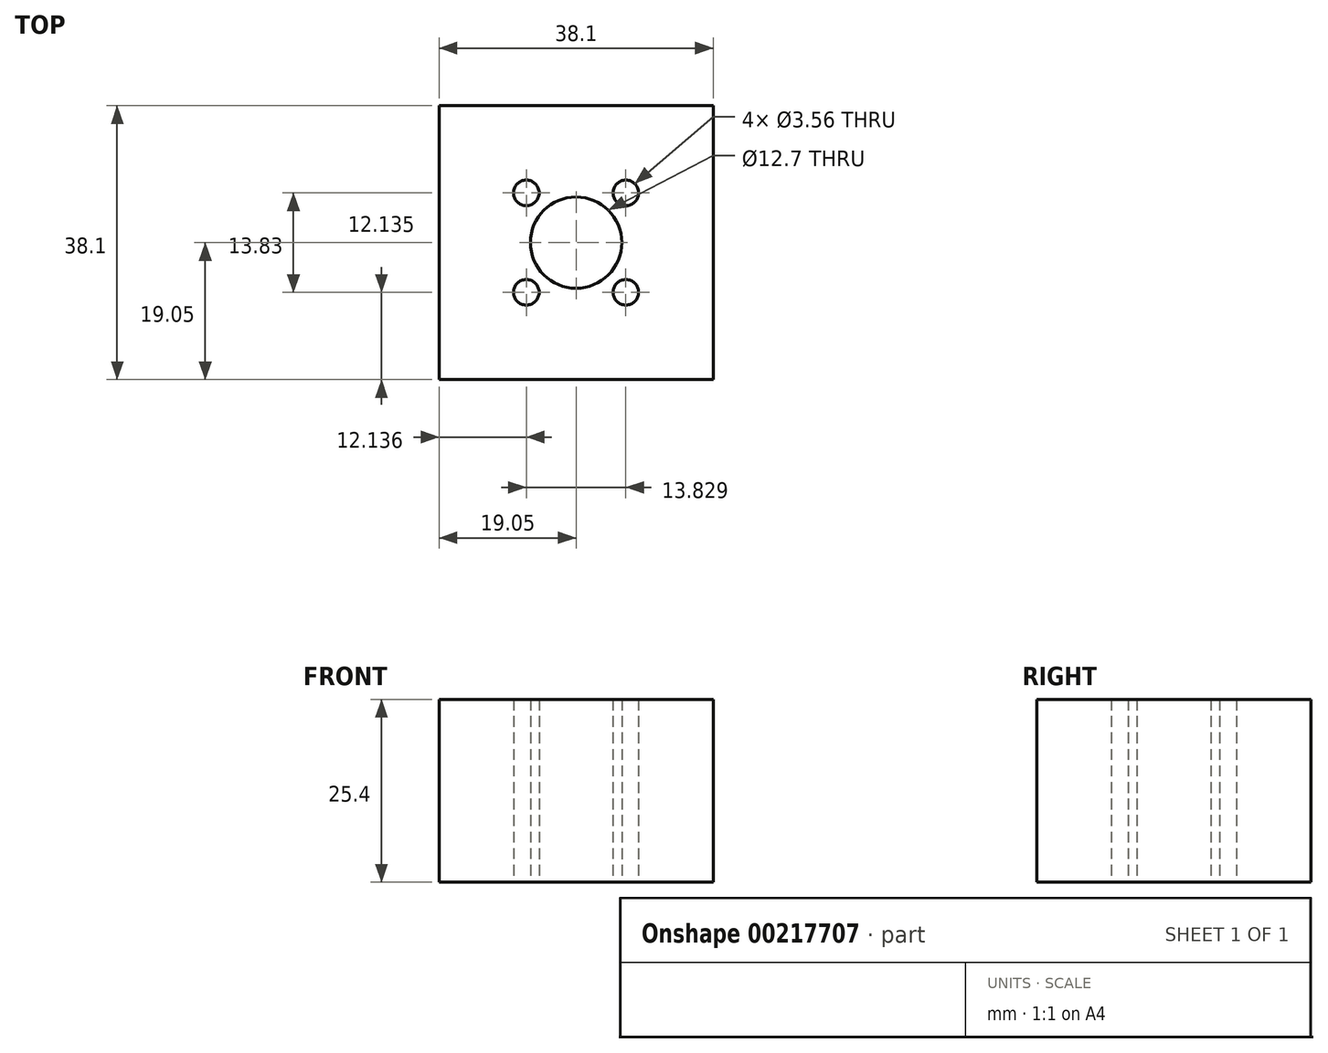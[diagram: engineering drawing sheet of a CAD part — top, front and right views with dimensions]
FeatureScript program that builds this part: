
annotation { "Feature Type Name" : "Feature", "Feature Type Description" : "" }
export const myFeature = defineFeature(function(context is Context, id is Id, definition is map)
    precondition{}
    {
        {
            var Q0;
            Q0=qCreatedBy(makeId("Top.planeOp"),FACE);
            var sketch = newSketch(context, id + "F0", { "sketchPlane" : qUnion([Q0])});
            skLineSegment(sketch, "E0.bottom", {"start": v(-19.05, 19.05) * mm, "end": v(19.05, 19.05) * mm});
            skLineSegment(sketch, "E0.top", {"start": v(-19.05, -19.05) * mm, "end": v(19.05, -19.05) * mm});
            skLineSegment(sketch, "E0.left", {"start": v(-19.05, 19.05) * mm, "end": v(-19.05, -19.05) * mm});
            skLineSegment(sketch, "E0.right", {"start": v(19.05, 19.05) * mm, "end": v(19.05, -19.05) * mm});
            skPoint(sketch, "E0.middle", {"position": v(0, 0) * mm});
            skCircle(sketch, "E1", {"center": v(0, 0) * mm, "radius": 6.35 * mm});
            skCircle(sketch, "E2", {"center": v(-6.91, 6.92) * mm, "radius": 1.78 * mm});
            skCircle(sketch, "E3", {"center": v(6.91, 6.92) * mm, "radius": 1.78 * mm});
            skCircle(sketch, "E4", {"center": v(6.91, -6.92) * mm, "radius": 1.78 * mm});
            skCircle(sketch, "E5", {"center": v(-6.91, -6.92) * mm, "radius": 1.78 * mm});
            skSolve(sketch);
        }
        {
            var Q0;
            Q0=makeQuery(id+"F0.imprint","IMPRINT",FACE,{"disambiguationData":[TD([[makeQuery(id+"F0.imprint","IMPRINT",EDGE,{"derivedFrom":sQuery(id+"F0.wireOp",EDGE,"E0.bottom")}),-1.0]])]});
            extrude(context, id + "F1", {"entities" : qUnion([Q0]), "depth" : 25.4 * mm});
        }
    });
